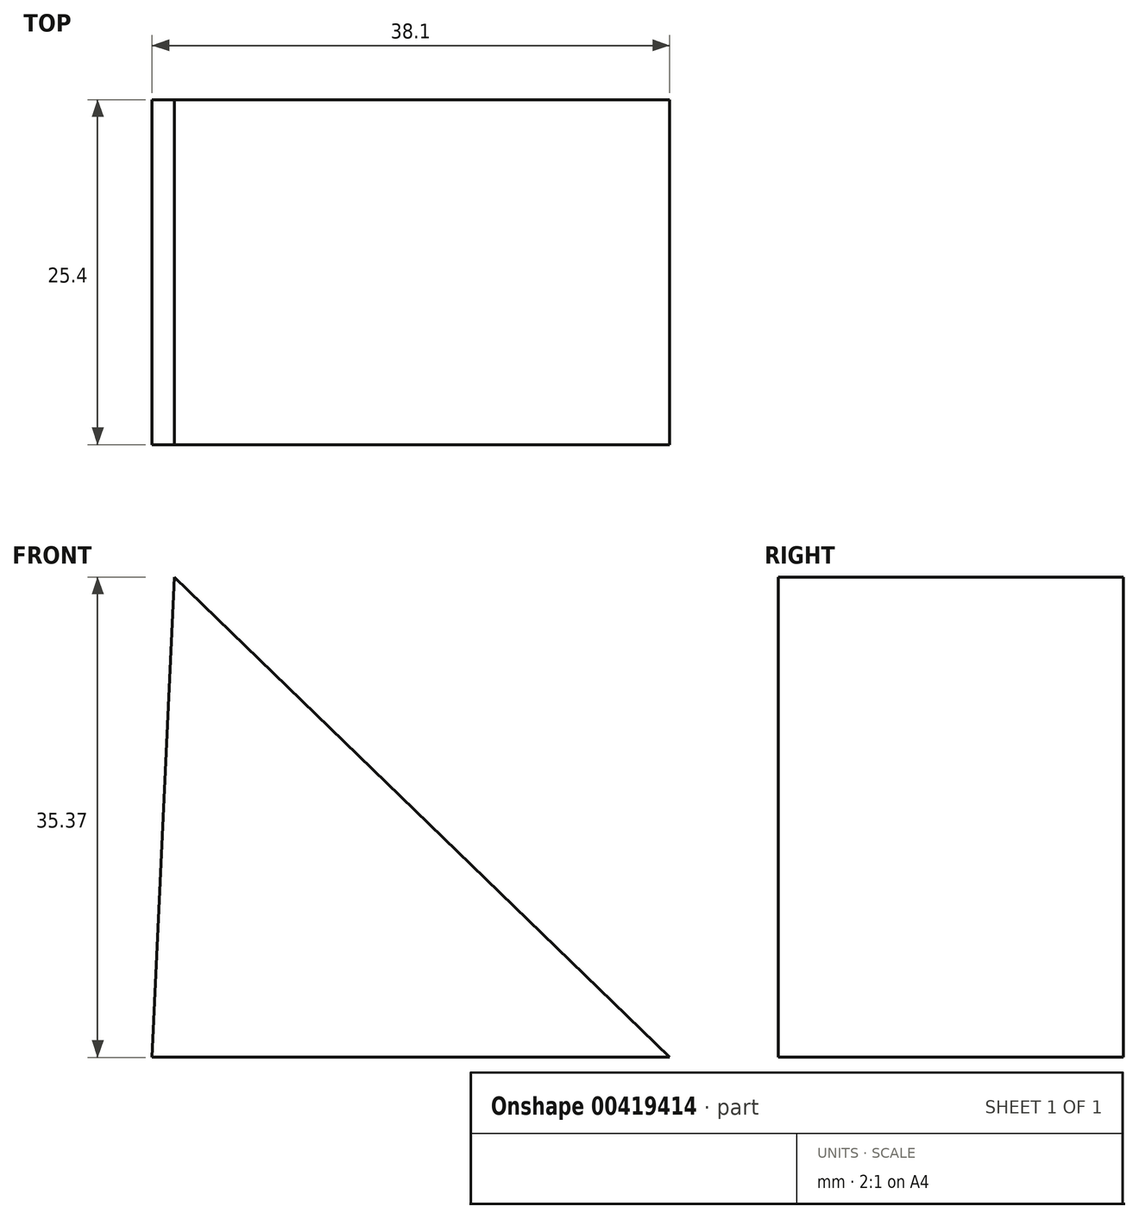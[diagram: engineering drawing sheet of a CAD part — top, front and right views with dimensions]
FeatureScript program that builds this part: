
annotation { "Feature Type Name" : "Feature", "Feature Type Description" : "" }
export const myFeature = defineFeature(function(context is Context, id is Id, definition is map)
    precondition{}
    {
        {
            var Q0;
            Q0=qCreatedBy(makeId("Front.planeOp"),FACE);
            var sketch = newSketch(context, id + "F0", { "sketchPlane" : qUnion([Q0])});
            skLineSegment(sketch, "E0", {"start": v(-67.87, 60.65) * mm, "end": v(-31.4, 25.28) * mm});
            skLineSegment(sketch, "E1", {"start": v(-31.4, 25.28) * mm, "end": v(-69.5, 25.28) * mm});
            skLineSegment(sketch, "E2", {"start": v(-67.87, 60.65) * mm, "end": v(-69.5, 25.28) * mm});
            skSolve(sketch);
        }
        {
            var Q0;
            Q0 = qSketchRegion(id + "F0", true);
            extrude(context, id + "F1", {"entities" : qUnion([Q0]), "depth" : 25.4 * mm});
        }
    });
